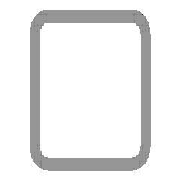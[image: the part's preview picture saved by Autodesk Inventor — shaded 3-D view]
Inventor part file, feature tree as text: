
AUTODESK INVENTOR PART (.ipt)
format: ipt  version: 2025 (Build 290162010, 162A)  size: 131,072 bytes
history: native  units: mm (DEFAULTED — no unit token found)
features: other x4, sketch x1, plane x1
ambient origin geometry x8: Origin, YZ Plane, XZ Plane, XY Plane, X Axis, Y Axis, Z Axis, Center Point
bodies: Solid1 (feature_tree), Body (feature_tree)
feature tree (6):
  parser-record x1  (decoder bookkeeping rows leaked as tree rows — omitted from the tree; the rows remain in map.json)
  other  "Driven Length"
  other  "Start Plane"
  other  "End Plane"
  sketch  "Sketch3"  dims[d3=1420.0mm d4=0.0mm d7=4.0mm d9=40.0mm d11=40.0mm d12=2.0mm d13=40.0mm d14=1460.0mm d15=20.0mm d16=20.0mm d17=90.0deg d18=1420.0mm]
  plane  "Work Plane3"
